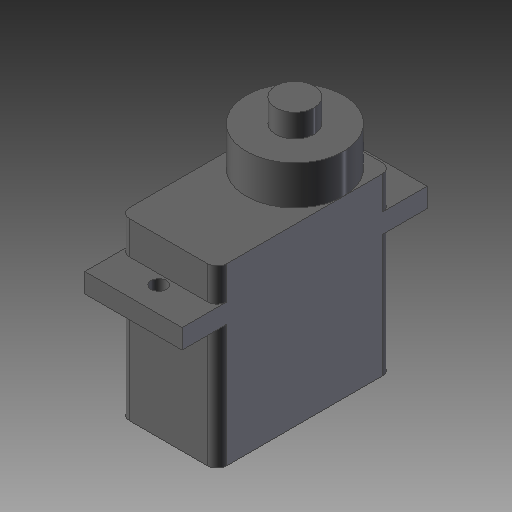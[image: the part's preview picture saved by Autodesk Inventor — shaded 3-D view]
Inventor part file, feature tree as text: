
AUTODESK INVENTOR PART (.ipt)
format: ipt  version: 2018 (Build 220112000, 112)  size: 146,432 bytes
history: native  units: in
note: dims shown in document units (in); Inventor stores cm internally (conversion verified against a paired STEP export)
features: sketch x5, other x3, plane x1
ambient origin geometry x8: Origin, YZ Plane, XZ Plane, XY Plane, X Axis, Y Axis, Z Axis, Center Point
bodies: Solid1 (feature_tree)
feature tree (9):
  other  "servo (2).ipt"
  other  "Solid1::servo (2).ipt"
  other  "TaggingFeature1"
  sketch  "Sketch1"  dims[d0=0.3937in]
  sketch  "Sketch2"
  sketch  "Sketch5"
  sketch  "Sketch6"
  sketch  "Sketch7"
  plane  "Work Plane1"
